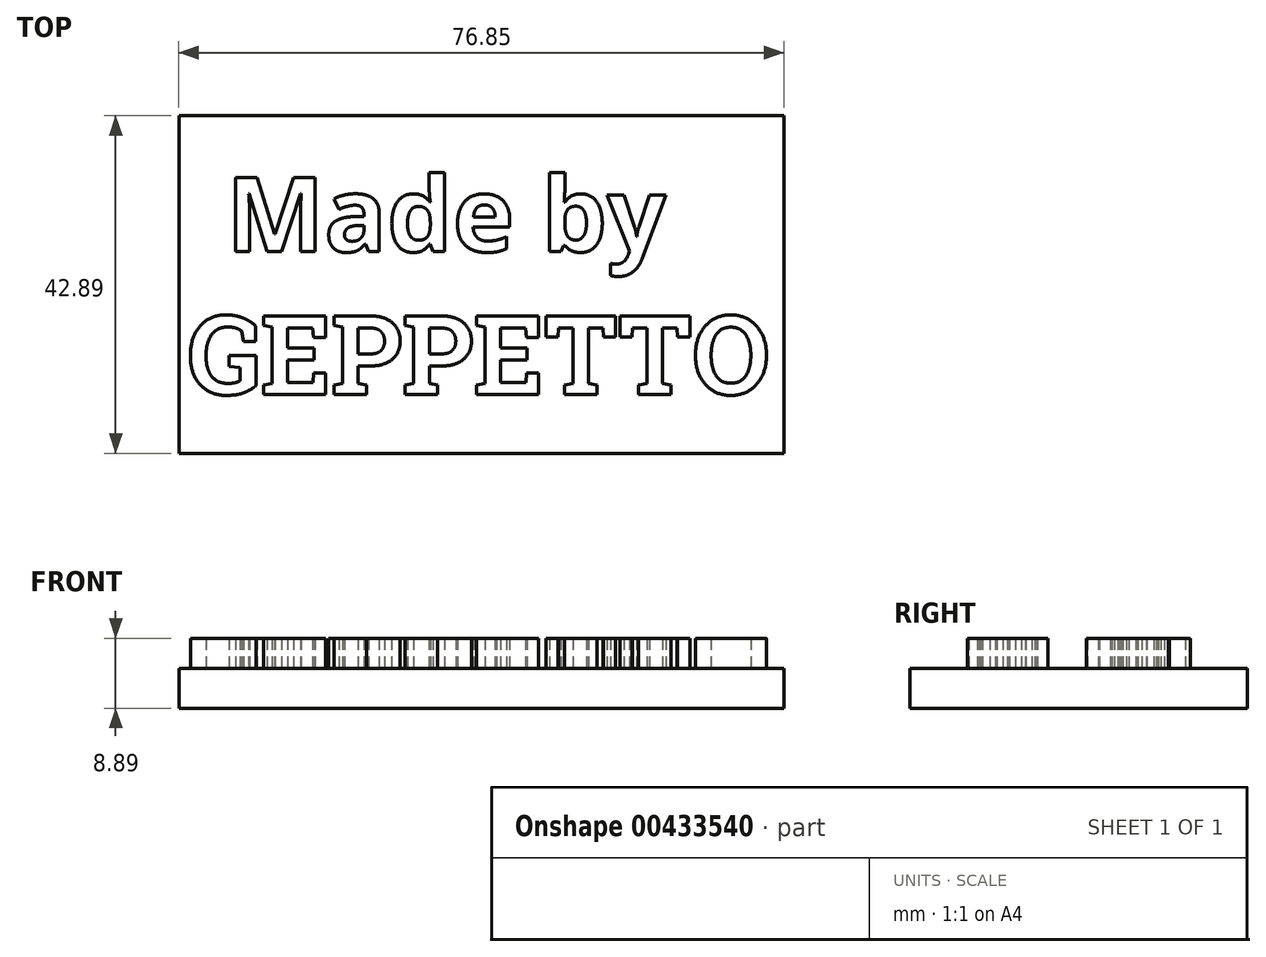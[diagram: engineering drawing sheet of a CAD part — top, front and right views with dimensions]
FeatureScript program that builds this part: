
annotation { "Feature Type Name" : "Feature", "Feature Type Description" : "" }
export const myFeature = defineFeature(function(context is Context, id is Id, definition is map)
    precondition{}
    {
        {
            var Q0;
            Q0=qCreatedBy(makeId("Top.planeOp"),FACE);
            var sketch = newSketch(context, id + "F0", { "sketchPlane" : qUnion([Q0])});
            skLineSegment(sketch, "E0.bottom", {"start": v(-30.8, 27.92) * mm, "end": v(46.05, 27.92) * mm});
            skLineSegment(sketch, "E0.top", {"start": v(-30.8, -14.97) * mm, "end": v(46.05, -14.97) * mm});
            skLineSegment(sketch, "E0.left", {"start": v(-30.8, 27.92) * mm, "end": v(-30.8, -14.97) * mm});
            skLineSegment(sketch, "E0.right", {"start": v(46.05, 27.92) * mm, "end": v(46.05, -14.97) * mm});
            skText(sketch, "E1", { "text": "GEPPETTO", "fontName": "DroidSansMono.ttf"});
            skText(sketch, "E2", { "text": "Made by\n", "fontName": "OpenSans-Bold.ttf"});
            const initialGuessF0  = {"E1": [-0.18074, -0.00345, 1, 0, 0.01065], "E2": [-0.16549, 0.02072, 1, 0, 0.00979]};
            skSetInitialGuess(sketch, initialGuessF0);
            skSolve(sketch);
        }
        {
            var Q0;
            Q0=makeQuery(id+"F0.imprint","IMPRINT",FACE,{"disambiguationData":[TD([[makeQuery(id+"F0.imprint","IMPRINT",EDGE,{"derivedFrom":sQuery(id+"F0.wireOp",EDGE,"E0.bottom")}),-1.0]])]});
            extrude(context, id + "F1", {"entities" : qUnion([Q0]), "depth" : 5.08 * mm});
        }
        {
            var Q0;
            Q0=makeQuery(id+"F1.opExtrude","CAP_FACE",FACE,{"disambiguationData":[OSD([sQuery(id+"F0.wireOp",EDGE,"E0.bottom"),sQuery(id+"F0.wireOp",EDGE,"E0.top"),sQuery(id+"F0.wireOp",EDGE,"E0.left"),sQuery(id+"F0.wireOp",EDGE,"E0.right")])],"isStart":false});
            var sketch = newSketch(context, id + "F2", { "sketchPlane" : qUnion([Q0])});
            skText(sketch, "E3", { "text": "Made by\n", "fontName": "OpenSans-Bold.ttf"});
            skText(sketch, "E4", { "text": "GEPPETTO", "fontName": "RobotoSlab-Bold.ttf"});
            const initialGuessF2  = {"E3": [-0.02475, 0.01065, 1, 0, 0.0095], "E4": [-0.02964, -0.00748, 1, 0, 0.01007]};
            skSetInitialGuess(sketch, initialGuessF2);
            skSolve(sketch);
        }
        {
            var Q0;
            Q0 = qSketchRegion(id + "F2", true);
            extrude(context, id + "F3", {"entities" : qUnion([Q0]), "operationType" : NewBodyOperationType.ADD, "depth" : 3.8 * mm});
        }
    });
